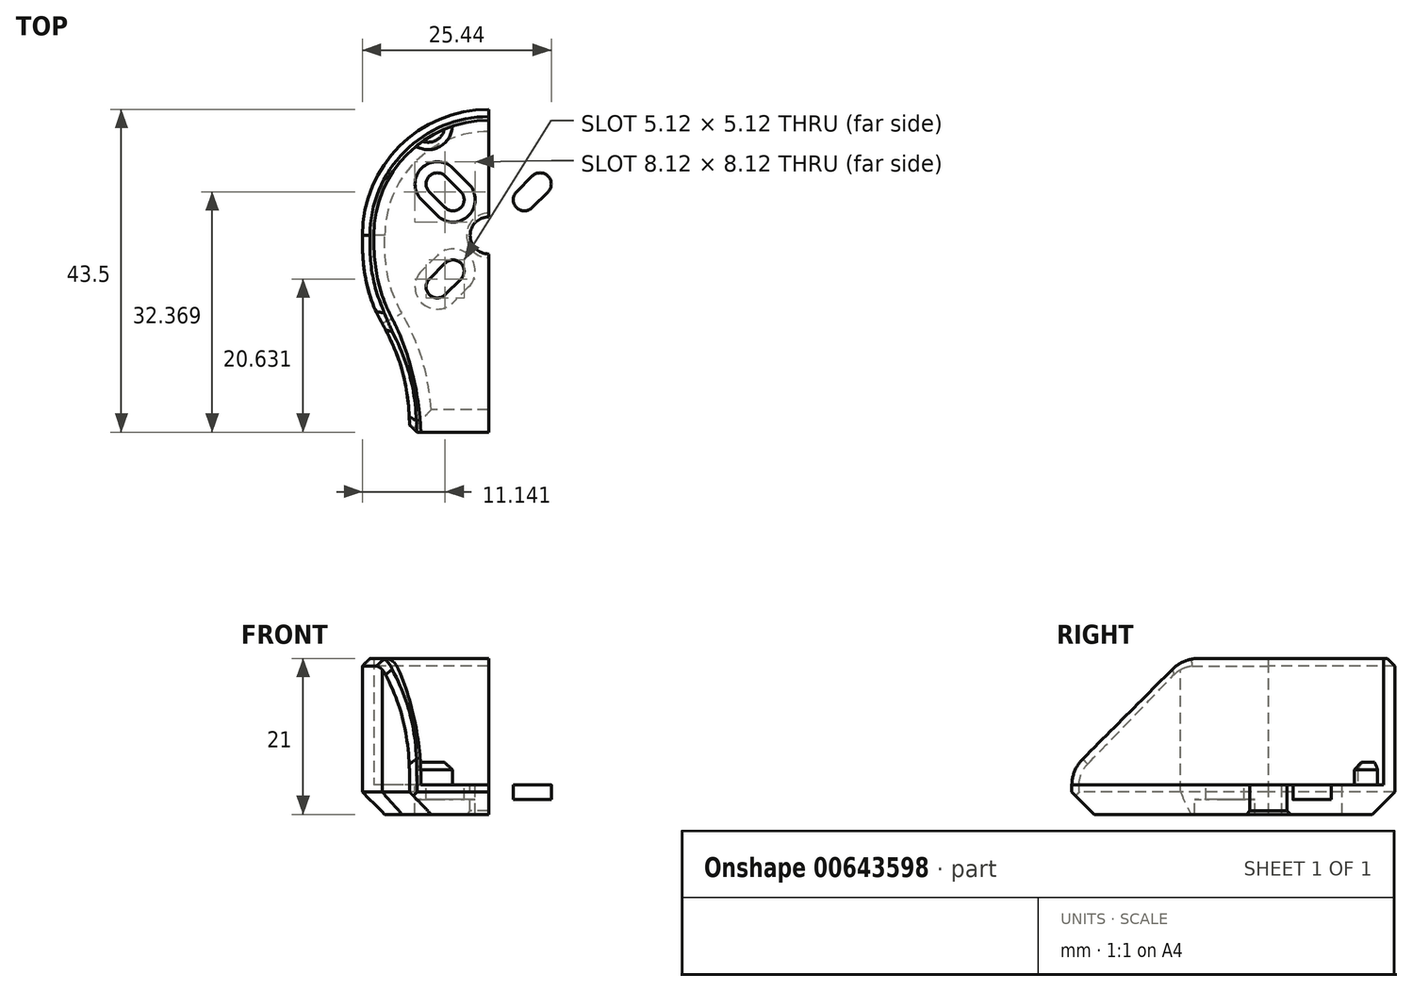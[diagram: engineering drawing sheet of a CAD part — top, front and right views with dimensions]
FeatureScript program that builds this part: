
annotation { "Feature Type Name" : "Feature", "Feature Type Description" : "" }
export const myFeature = defineFeature(function(context is Context, id is Id, definition is map)
    precondition{}
    {
        {
            var Q0;
            Q0=qCreatedBy(makeId("Top.planeOp"),FACE);
            var sketch = newSketch(context, id + "F0", { "sketchPlane" : qUnion([Q0])});
            skLineSegment(sketch, "E0", {"start": v(0, 15.5) * mm, "end": v(0, -26.5) * mm});
            skArc(sketch, "E1", {"start": v(0, 2.5) * mm, "mid": v(-2.5, 0) * mm, "end": v(0, -2.5) * mm});
            skLineSegment(sketch, "E2", {"start": v(0, 0) * mm, "end": v(-8, 8) * mm, "construction": true});
            skArc(sketch, "E3", {"start": v(-8, 8) * mm, "mid": v(-6.93, 8.43) * mm, "end": v(-5.87, 8) * mm});
            skArc(sketch, "E4", {"start": v(-3.75, 3.75) * mm, "mid": v(-3.3, 4.8) * mm, "end": v(-3.75, 5.87) * mm});
            skLineSegment(sketch, "E5", {"start": v(-3.75, 5.87) * mm, "end": v(-5.87, 8) * mm});
            skLineSegment(sketch, "E6", {"start": v(-6.93, 6.93) * mm, "end": v(-5.87, 8) * mm, "construction": true});
            skArc(sketch, "E7.MirrorCS", {"start": v(-8, 8) * mm, "mid": v(-8.43, 6.93) * mm, "end": v(-8, 5.87) * mm});
            skLineSegment(sketch, "E8.MirrorCS", {"start": v(-5.87, 3.75) * mm, "end": v(-8, 5.87) * mm});
            skArc(sketch, "E9.MirrorCS", {"start": v(-3.75, 3.75) * mm, "mid": v(-4.8, 3.3) * mm, "end": v(-5.87, 3.75) * mm});
            skArc(sketch, "E10.MirrorCS", {"start": v(-3.75, -3.75) * mm, "mid": v(-4.8, -3.3) * mm, "end": v(-5.87, -3.75) * mm});
            skArc(sketch, "E11.MirrorCS", {"start": v(-3.75, -3.75) * mm, "mid": v(-3.3, -4.8) * mm, "end": v(-3.75, -5.87) * mm});
            skLineSegment(sketch, "E12.MirrorCS", {"start": v(-3.75, -5.87) * mm, "end": v(-5.87, -8) * mm});
            skLineSegment(sketch, "E13.MirrorCS", {"start": v(-5.87, -3.75) * mm, "end": v(-8, -5.87) * mm});
            skArc(sketch, "E14.MirrorCS", {"start": v(-8, -8) * mm, "mid": v(-8.43, -6.93) * mm, "end": v(-8, -5.87) * mm});
            skArc(sketch, "E15.MirrorCS", {"start": v(-8, -8) * mm, "mid": v(-6.93, -8.43) * mm, "end": v(-5.87, -8) * mm});
            skArc(sketch, "E16", {"start": v(0, -14) * mm, "mid": v(-14, 0) * mm, "end": v(0, 14) * mm, "construction": true});
            skLineSegment(sketch, "E17", {"start": v(-9.15, -26.5) * mm, "end": v(0, -26.5) * mm});
            skArc(sketch, "E18.0", {"start": v(-9.05, 9.05) * mm, "mid": v(-9.93, 6.93) * mm, "end": v(-9.05, 4.8) * mm});
            skLineSegment(sketch, "E18.1", {"start": v(-2.69, 6.93) * mm, "end": v(-4.8, 9.05) * mm});
            skArc(sketch, "E18.2", {"start": v(-2.69, 2.69) * mm, "mid": v(-1.8, 4.8) * mm, "end": v(-2.69, 6.93) * mm});
            skArc(sketch, "E18.3", {"start": v(-9.05, 9.05) * mm, "mid": v(-6.93, 9.93) * mm, "end": v(-4.8, 9.05) * mm});
            skArc(sketch, "E18.4", {"start": v(-2.69, 2.69) * mm, "mid": v(-4.8, 1.8) * mm, "end": v(-6.93, 2.69) * mm});
            skLineSegment(sketch, "E18.5", {"start": v(-6.93, 2.69) * mm, "end": v(-9.05, 4.8) * mm});
            skArc(sketch, "E19.MirrorCS", {"start": v(-9.05, -9.05) * mm, "mid": v(-6.93, -9.93) * mm, "end": v(-4.8, -9.05) * mm});
            skArc(sketch, "E20.MirrorCS", {"start": v(-9.05, -9.05) * mm, "mid": v(-9.93, -6.93) * mm, "end": v(-9.05, -4.8) * mm});
            skLineSegment(sketch, "E21.MirrorCS", {"start": v(-6.93, -2.69) * mm, "end": v(-9.05, -4.8) * mm});
            skArc(sketch, "E22.MirrorCS", {"start": v(-2.69, -2.69) * mm, "mid": v(-4.8, -1.8) * mm, "end": v(-6.93, -2.69) * mm});
            skArc(sketch, "E23.MirrorCS", {"start": v(-2.69, -2.69) * mm, "mid": v(-1.8, -4.8) * mm, "end": v(-2.69, -6.93) * mm});
            skLineSegment(sketch, "E24.MirrorCS", {"start": v(-2.69, -6.93) * mm, "end": v(-4.8, -9.05) * mm});
            skArc(sketch, "E25", {"start": v(0, 15.5) * mm, "mid": v(-10.96, 10.96) * mm, "end": v(-15.5, 0) * mm});
            skFitSpline(sketch, "E26", {"points": [v(-9.15, -26.5) * mm, v(-13, -11.2) * mm], "startDerivative": vector(-0.59, 16.7) * mm, "endDerivative": vector(-6.42, 12.49) * mm});
            skFitSpline(sketch, "E27", {"points": [v(-13, -11.2) * mm, v(-15.5, 0) * mm], "startDerivative": vector(-2.9, 5.58) * mm, "endDerivative": vector(0, 18.88) * mm});
            skFitSpline(sketch, "E28.0", {"points": [v(-10.65, -26.55) * mm, v(-10.74, -23.89) * mm, v(-11.57, -18.52) * mm, v(-13.32, -13.85) * mm, v(-14.33, -11.89) * mm]});
            skFitSpline(sketch, "E28.1", {"points": [v(-14.33, -11.9) * mm, v(-14.58, -11.42) * mm, v(-15.17, -10.27) * mm, v(-16.1, -7.81) * mm, v(-16.8, -4.5) * mm, v(-17, -1.63) * mm, v(-17, 0) * mm]});
            skArc(sketch, "E28.2", {"start": v(0, 17) * mm, "mid": v(-12.02, 12.02) * mm, "end": v(-17, 0) * mm});
            skLineSegment(sketch, "E29", {"start": v(-9.15, -26.5) * mm, "end": v(-10.65, -26.5) * mm});
            skLineSegment(sketch, "E30", {"start": v(0, 17) * mm, "end": v(0, 15.5) * mm});
            skArc(sketch, "E31", {"start": v(-9.8, 12) * mm, "mid": v(-6.58, 11.95) * mm, "end": v(-4.9, 14.7) * mm});
            skLineSegment(sketch, "E32", {"start": v(-4.9, 14.7) * mm, "end": v(-9.8, 12) * mm, "construction": true});
            skSolve(sketch);
        }
        {
            var Q0;
            Q0=makeQuery(id+"F0.imprint","IMPRINT",FACE,{"disambiguationData":[TD([[makeQuery(id+"F0.imprint","IMPRINT",EDGE,{"derivedFrom":sQuery(id+"F0.wireOp",EDGE,"E26")}),1.0]])]});
            var Q1;
            {var subQ0=sQuery(id+"F0.wireOp",EDGE,"E31");Q1=makeQuery(id+"F0.imprint","IMPRINT",FACE,{"disambiguationData":[TD([[makeQuery(id+"F0.imprint","IMPRINT",EDGE,{"derivedFrom":subQ0}),1.0]])]});}
            var Q2;
            {var subQ3=sQuery(id+"F0.wireOp",EDGE,"E1");Q2=makeQuery(id+"F0.imprint","IMPRINT",FACE,{"disambiguationData":[TD([[makeQuery(id+"F0.imprint","IMPRINT",EDGE,{"derivedFrom":subQ3}),-1.0]])]});}
            var Q3;
            Q3=makeQuery(id+"F0.imprint","IMPRINT",FACE,{"disambiguationData":[TD([[makeQuery(id+"F0.imprint","IMPRINT",EDGE,{"derivedFrom":sQuery(id+"F0.wireOp",EDGE,"E3")}),1.0]])]});
            var Q4;
            Q4=makeQuery(id+"F0.imprint","IMPRINT",FACE,{"disambiguationData":[TD([[makeQuery(id+"F0.imprint","IMPRINT",EDGE,{"derivedFrom":sQuery(id+"F0.wireOp",EDGE,"E10.MirrorCS")}),-1.0]])]});
            extrude(context, id + "F1", {"entities" : qUnion([Q0, Q1, Q2, Q3, Q4]), "oppositeDirection" : true, "depth" : 4 * mm, "offsetDistance" : 25 * mm});
        }
        {
            var Q0;
            Q0=makeQuery(id+"F0.imprint","IMPRINT",FACE,{"disambiguationData":[TD([[makeQuery(id+"F0.imprint","IMPRINT",EDGE,{"derivedFrom":sQuery(id+"F0.wireOp",EDGE,"E26")}),1.0]])]});
            extrude(context, id + "F2", {"entities" : qUnion([Q0]), "operationType" : NewBodyOperationType.ADD, "depth" : 17 * mm, "offsetDistance" : 25 * mm});
        }
        {
            var Q0;
            {var subQ0=sQuery(id+"F0.wireOp",EDGE,"E31");Q0=makeQuery(id+"F0.imprint","IMPRINT",FACE,{"disambiguationData":[TD([[makeQuery(id+"F0.imprint","IMPRINT",EDGE,{"derivedFrom":subQ0}),1.0]])]});}
            extrude(context, id + "F3", {"entities" : qUnion([Q0]), "operationType" : NewBodyOperationType.ADD, "depth" : 3 * mm, "offsetDistance" : 25 * mm});
        }
        {
            var Q0;
            Q0=makeQuery(id+"F3.opExtrude","CAP_EDGE",EDGE,{"disambiguationData":[OSD([sQuery(id+"F0.wireOp",EDGE,"E31")])],"isStart":false});
            chamfer(context, id + "F4", {"entities" : qUnion([Q0]), "width" : 1 * mm, "tangentPropagation" : true});
        }
        {
            var Q0;
            Q0=makeQuery(id+"F0.imprint","IMPRINT",FACE,{"disambiguationData":[TD([[makeQuery(id+"F0.imprint","IMPRINT",EDGE,{"derivedFrom":sQuery(id+"F0.wireOp",EDGE,"E10.MirrorCS")}),-1.0]])]});
            var Q1;
            Q1=makeQuery(id+"F0.imprint","IMPRINT",FACE,{"disambiguationData":[TD([[makeQuery(id+"F0.imprint","IMPRINT",EDGE,{"derivedFrom":sQuery(id+"F0.wireOp",EDGE,"E3")}),1.0]])]});
            extrude(context, id + "F5", {"entities" : qUnion([Q0, Q1]), "operationType" : NewBodyOperationType.REMOVE, "endBound" : BoundingType.THROUGH_ALL, "oppositeDirection" : true, "depth" : 25 * mm, "offsetDistance" : 25 * mm, "hasSecondDirection" : true, "secondDirectionOppositeDirection" : true, "secondDirectionDepth" : 2 * mm});
        }
        {
            var Q0;
            Q0=makeQuery(id+"F1.opExtrude","CAP_EDGE",EDGE,{"disambiguationData":[OSD([sQuery(id+"F0.wireOp",EDGE,"E28.0")])],"isStart":false});
            var Q1;
            Q1=makeQuery(id+"F1.opExtrude","CAP_EDGE",EDGE,{"disambiguationData":[OSD([sQuery(id+"F0.wireOp",EDGE,"E17"),sQuery(id+"F0.wireOp",EDGE,"E29")])],"isStart":false});
            var Q2;
            Q2=makeQuery(id+"F1.opExtrude","CAP_EDGE",EDGE,{"disambiguationData":[OSD([sQuery(id+"F0.wireOp",EDGE,"E28.2")])],"isStart":false});
            chamfer(context, id + "F6", {"entities" : qUnion([Q0, Q1, Q2]), "width" : 3 * mm, "tangentPropagation" : true});
        }
        {
            var Q0;
            Q0=makeQuery(id+"F2.opExtrude","CAP_EDGE",EDGE,{"disambiguationData":[OSD([sQuery(id+"F0.wireOp",EDGE,"E29")])],"isStart":false});
            chamfer(context, id + "F7", {"entities" : qUnion([Q0]), "width" : 15 * mm, "tangentPropagation" : true});
        }
        {
            var Q0;
            {var subQ0=sQuery(id+"F0.wireOp",EDGE,"E29");Q0=makeQuery(id+"F7.opChamfer","BLEND_EDGE",EDGE,{"blendedFrom":[makeQuery(id+"F2.opExtrude","CAP_EDGE",EDGE,{"disambiguationData":[OSD([subQ0])],"isStart":false}),makeQuery(id+"F2.boolean.opBoolean","MERGE",FACE,{"derivedFrom":[makeQuery(id+"F1.opExtrude","SWEPT_FACE",FACE,{"disambiguationData":[OSD([sQuery(id+"F0.wireOp",EDGE,"E17"),subQ0])]}),makeQuery(id+"F2.opExtrude","SWEPT_FACE",FACE,{"disambiguationData":[OSD([subQ0])]})]})],"blendedInto":[makeQuery(id+"F2.boolean.opBoolean","MERGE",FACE,{"derivedFrom":[makeQuery(id+"F1.opExtrude","SWEPT_FACE",FACE,{"disambiguationData":[OSD([sQuery(id+"F0.wireOp",EDGE,"E17"),subQ0])]}),makeQuery(id+"F2.opExtrude","SWEPT_FACE",FACE,{"disambiguationData":[OSD([subQ0])]})]})]});}
            var Q1;
            {var subQ0=sQuery(id+"F0.wireOp",EDGE,"E29");Q1=makeQuery(id+"F7.opChamfer","BLEND_EDGE",EDGE,{"blendedFrom":[makeQuery(id+"F2.opExtrude","CAP_EDGE",EDGE,{"disambiguationData":[OSD([subQ0])],"isStart":false}),makeQuery(id+"F2.opExtrude","CAP_FACE",FACE,{"disambiguationData":[OSD([sQuery(id+"F0.wireOp",EDGE,"E25"),sQuery(id+"F0.wireOp",EDGE,"E26"),sQuery(id+"F0.wireOp",EDGE,"E27"),sQuery(id+"F0.wireOp",EDGE,"E28.0"),sQuery(id+"F0.wireOp",EDGE,"E28.1"),sQuery(id+"F0.wireOp",EDGE,"E28.2"),subQ0,sQuery(id+"F0.wireOp",EDGE,"E30")])],"isStart":false})],"blendedInto":[makeQuery(id+"F2.opExtrude","CAP_FACE",FACE,{"disambiguationData":[OSD([sQuery(id+"F0.wireOp",EDGE,"E25"),sQuery(id+"F0.wireOp",EDGE,"E26"),sQuery(id+"F0.wireOp",EDGE,"E27"),sQuery(id+"F0.wireOp",EDGE,"E28.0"),sQuery(id+"F0.wireOp",EDGE,"E28.1"),sQuery(id+"F0.wireOp",EDGE,"E28.2"),subQ0,sQuery(id+"F0.wireOp",EDGE,"E30")])],"isStart":false})]});}
            fillet(context, id + "F8", {"entities" : qUnion([Q0, Q1]), "radius" : 5 * mm, "tangentPropagation" : true, "allowEdgeOverflow" : false});
        }
        {
            var Q0;
            Q0=makeQuery(id+"F5.boolean.opBoolean","INTERSECT",EDGE,{"derivedFrom":[makeQuery(id+"F1.opExtrude","CAP_FACE",FACE,{"disambiguationData":[OSD([sQuery(id+"F0.wireOp",EDGE,"E0"),sQuery(id+"F0.wireOp",EDGE,"E1"),sQuery(id+"F0.wireOp",EDGE,"E3"),sQuery(id+"F0.wireOp",EDGE,"E4"),sQuery(id+"F0.wireOp",EDGE,"E5"),sQuery(id+"F0.wireOp",EDGE,"E7.MirrorCS"),sQuery(id+"F0.wireOp",EDGE,"E8.MirrorCS"),sQuery(id+"F0.wireOp",EDGE,"E9.MirrorCS"),sQuery(id+"F0.wireOp",EDGE,"E10.MirrorCS"),sQuery(id+"F0.wireOp",EDGE,"E11.MirrorCS"),sQuery(id+"F0.wireOp",EDGE,"E12.MirrorCS"),sQuery(id+"F0.wireOp",EDGE,"E13.MirrorCS"),sQuery(id+"F0.wireOp",EDGE,"E14.MirrorCS"),sQuery(id+"F0.wireOp",EDGE,"E15.MirrorCS"),sQuery(id+"F0.wireOp",EDGE,"c450db0a-ccab-4600-98b1-c0642d316d13.0"),sQuery(id+"F0.wireOp",EDGE,"c450db0a-ccab-4600-98b1-c0642d316d13.1"),sQuery(id+"F0.wireOp",EDGE,"c450db0a-ccab-4600-98b1-c0642d316d13.2"),sQuery(id+"F0.wireOp",EDGE,"c450db0a-ccab-4600-98b1-c0642d316d13.3"),sQuery(id+"F0.wireOp",EDGE,"EIgGEZvk-Qm3d-RHmz-GvMt-O3KuvaaLzt5b"),sQuery(id+"F0.wireOp",EDGE,"mVhr3F3F-W4MW-MuDG-g2WE-mm2qOT6b9upe"),sQuery(id+"F0.wireOp",EDGE,"E17")])],"isStart":false}),makeQuery(id+"F5.opExtrude","SWEPT_FACE",FACE,{"disambiguationData":[OSD([sQuery(id+"F0.wireOp",EDGE,"E19.MirrorCS"),sQuery(id+"F0.wireOp",EDGE,"E20.MirrorCS")])]})]});
            var Q1;
            Q1=makeQuery(id+"F5.boolean.opBoolean","INTERSECT",EDGE,{"derivedFrom":[makeQuery(id+"F1.opExtrude","CAP_FACE",FACE,{"disambiguationData":[OSD([sQuery(id+"F0.wireOp",EDGE,"E0"),sQuery(id+"F0.wireOp",EDGE,"E1"),sQuery(id+"F0.wireOp",EDGE,"E3"),sQuery(id+"F0.wireOp",EDGE,"E4"),sQuery(id+"F0.wireOp",EDGE,"E5"),sQuery(id+"F0.wireOp",EDGE,"E7.MirrorCS"),sQuery(id+"F0.wireOp",EDGE,"E8.MirrorCS"),sQuery(id+"F0.wireOp",EDGE,"E9.MirrorCS"),sQuery(id+"F0.wireOp",EDGE,"E10.MirrorCS"),sQuery(id+"F0.wireOp",EDGE,"E11.MirrorCS"),sQuery(id+"F0.wireOp",EDGE,"E12.MirrorCS"),sQuery(id+"F0.wireOp",EDGE,"E13.MirrorCS"),sQuery(id+"F0.wireOp",EDGE,"E14.MirrorCS"),sQuery(id+"F0.wireOp",EDGE,"E15.MirrorCS"),sQuery(id+"F0.wireOp",EDGE,"c450db0a-ccab-4600-98b1-c0642d316d13.0"),sQuery(id+"F0.wireOp",EDGE,"c450db0a-ccab-4600-98b1-c0642d316d13.1"),sQuery(id+"F0.wireOp",EDGE,"c450db0a-ccab-4600-98b1-c0642d316d13.2"),sQuery(id+"F0.wireOp",EDGE,"c450db0a-ccab-4600-98b1-c0642d316d13.3"),sQuery(id+"F0.wireOp",EDGE,"EIgGEZvk-Qm3d-RHmz-GvMt-O3KuvaaLzt5b"),sQuery(id+"F0.wireOp",EDGE,"mVhr3F3F-W4MW-MuDG-g2WE-mm2qOT6b9upe"),sQuery(id+"F0.wireOp",EDGE,"E17")])],"isStart":false}),makeQuery(id+"F5.opExtrude","SWEPT_FACE",FACE,{"disambiguationData":[OSD([sQuery(id+"F0.wireOp",EDGE,"E18.0"),sQuery(id+"F0.wireOp",EDGE,"E18.3")])]})]});
            var Q2;
            Q2=makeQuery(id+"F1.opExtrude","CAP_EDGE",EDGE,{"disambiguationData":[OSD([sQuery(id+"F0.wireOp",EDGE,"E1")])],"isStart":false});
            chamfer(context, id + "F9", {"entities" : qUnion([Q0, Q1, Q2]), "width" : 0.5 * mm, "tangentPropagation" : true});
        }
        {
            var Q0;
            Q0=makeQuery(id+"F2.opExtrude","CAP_EDGE",EDGE,{"disambiguationData":[OSD([sQuery(id+"F0.wireOp",EDGE,"E28.2")])],"isStart":false});
            var Q1;
            {var subQ0=sQuery(id+"F0.wireOp",EDGE,"E28.0");Q1=makeQuery(id+"F7.opChamfer","BLEND_EDGE",EDGE,{"blendedFrom":[makeQuery(id+"F2.opExtrude","CAP_EDGE",EDGE,{"disambiguationData":[OSD([sQuery(id+"F0.wireOp",EDGE,"E29")])],"isStart":false}),makeQuery(id+"F2.boolean.opBoolean","MERGE",FACE,{"derivedFrom":[makeQuery(id+"F1.opExtrude","SWEPT_FACE",FACE,{"disambiguationData":[OSD([subQ0])]}),makeQuery(id+"F2.opExtrude","SWEPT_FACE",FACE,{"disambiguationData":[OSD([subQ0])]})]})],"blendedInto":[makeQuery(id+"F2.boolean.opBoolean","MERGE",FACE,{"derivedFrom":[makeQuery(id+"F1.opExtrude","SWEPT_FACE",FACE,{"disambiguationData":[OSD([subQ0])]}),makeQuery(id+"F2.opExtrude","SWEPT_FACE",FACE,{"disambiguationData":[OSD([subQ0])]})]})]});}
            chamfer(context, id + "F10", {"entities" : qUnion([Q0, Q1]), "width" : 1 * mm, "tangentPropagation" : true});
        }
        {
            var Q0;
            Q0=makeQuery(id+"F1.opExtrude","SWEPT_BODY",BODY,{"disambiguationData":[OSD([sQuery(id+"F0.wireOp",EDGE,"E0"),sQuery(id+"F0.wireOp",EDGE,"E1"),sQuery(id+"F0.wireOp",EDGE,"E3"),sQuery(id+"F0.wireOp",EDGE,"E4"),sQuery(id+"F0.wireOp",EDGE,"E5"),sQuery(id+"F0.wireOp",EDGE,"E7.MirrorCS"),sQuery(id+"F0.wireOp",EDGE,"E8.MirrorCS"),sQuery(id+"F0.wireOp",EDGE,"E9.MirrorCS"),sQuery(id+"F0.wireOp",EDGE,"E10.MirrorCS"),sQuery(id+"F0.wireOp",EDGE,"E11.MirrorCS"),sQuery(id+"F0.wireOp",EDGE,"E12.MirrorCS"),sQuery(id+"F0.wireOp",EDGE,"E13.MirrorCS"),sQuery(id+"F0.wireOp",EDGE,"E14.MirrorCS"),sQuery(id+"F0.wireOp",EDGE,"E15.MirrorCS"),sQuery(id+"F0.wireOp",EDGE,"c450db0a-ccab-4600-98b1-c0642d316d13.0"),sQuery(id+"F0.wireOp",EDGE,"c450db0a-ccab-4600-98b1-c0642d316d13.1"),sQuery(id+"F0.wireOp",EDGE,"c450db0a-ccab-4600-98b1-c0642d316d13.2"),sQuery(id+"F0.wireOp",EDGE,"c450db0a-ccab-4600-98b1-c0642d316d13.3"),sQuery(id+"F0.wireOp",EDGE,"EIgGEZvk-Qm3d-RHmz-GvMt-O3KuvaaLzt5b"),sQuery(id+"F0.wireOp",EDGE,"mVhr3F3F-W4MW-MuDG-g2WE-mm2qOT6b9upe"),sQuery(id+"F0.wireOp",EDGE,"E17")])]});
            var Q1;
            Q1=qCreatedBy(makeId("Right.planeOp"),FACE);
            mirror(context, id + "F11", {"operationType" : NewBodyOperationType.ADD, "entities" : qUnion([Q0]), "mirrorPlane" : qUnion([Q1])});
        }
    });
